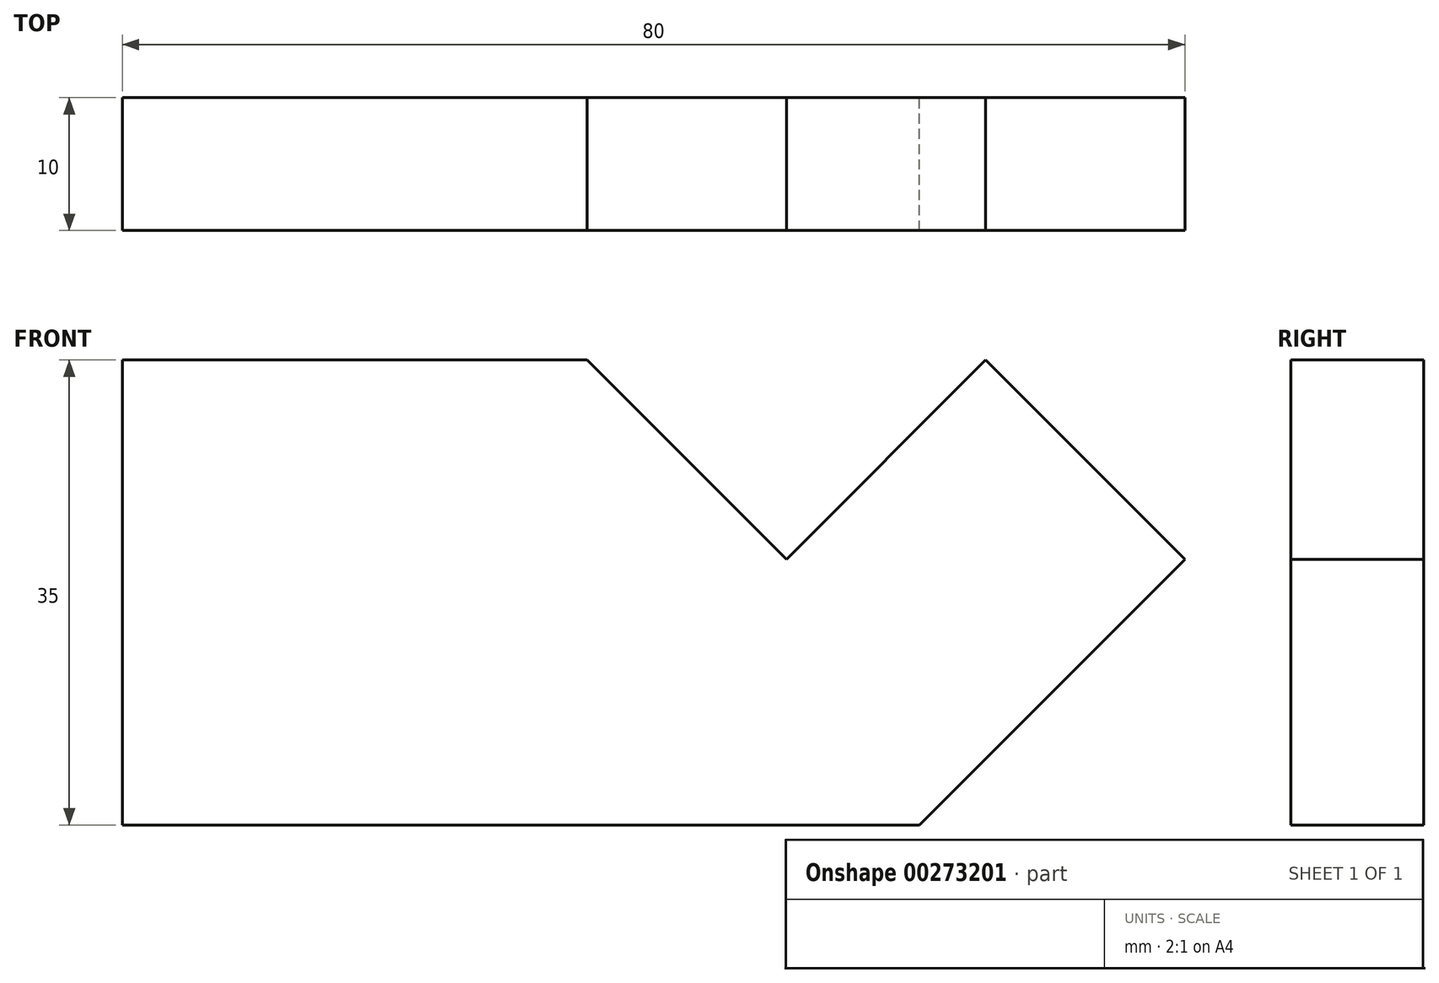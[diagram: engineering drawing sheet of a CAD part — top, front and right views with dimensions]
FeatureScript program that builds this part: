
annotation { "Feature Type Name" : "Feature", "Feature Type Description" : "" }
export const myFeature = defineFeature(function(context is Context, id is Id, definition is map)
    precondition{}
    {
        {
            var Q0;
            Q0=qCreatedBy(makeId("Front.planeOp"),FACE);
            var sketch = newSketch(context, id + "F0", { "sketchPlane" : qUnion([Q0])});
            skLineSegment(sketch, "E0", {"start": v(0, 0) * mm, "end": v(60, 0) * mm});
            skLineSegment(sketch, "E1", {"start": v(0, 0) * mm, "end": v(0, 35) * mm});
            skLineSegment(sketch, "E2", {"start": v(60, 0) * mm, "end": v(80, 20) * mm});
            skLineSegment(sketch, "E3", {"start": v(80, 20) * mm, "end": v(65, 35) * mm});
            skLineSegment(sketch, "E4", {"start": v(65, 35) * mm, "end": v(50, 20) * mm});
            skLineSegment(sketch, "E5", {"start": v(50, 20) * mm, "end": v(35, 35) * mm});
            skLineSegment(sketch, "E6", {"start": v(0, 35) * mm, "end": v(35, 35) * mm});
            skSolve(sketch);
        }
        {
            var Q0;
            Q0 = qSketchRegion(id + "F0", true);
            extrude(context, id + "F1", {"entities" : qUnion([Q0]), "depth" : 10 * mm});
        }
    });
